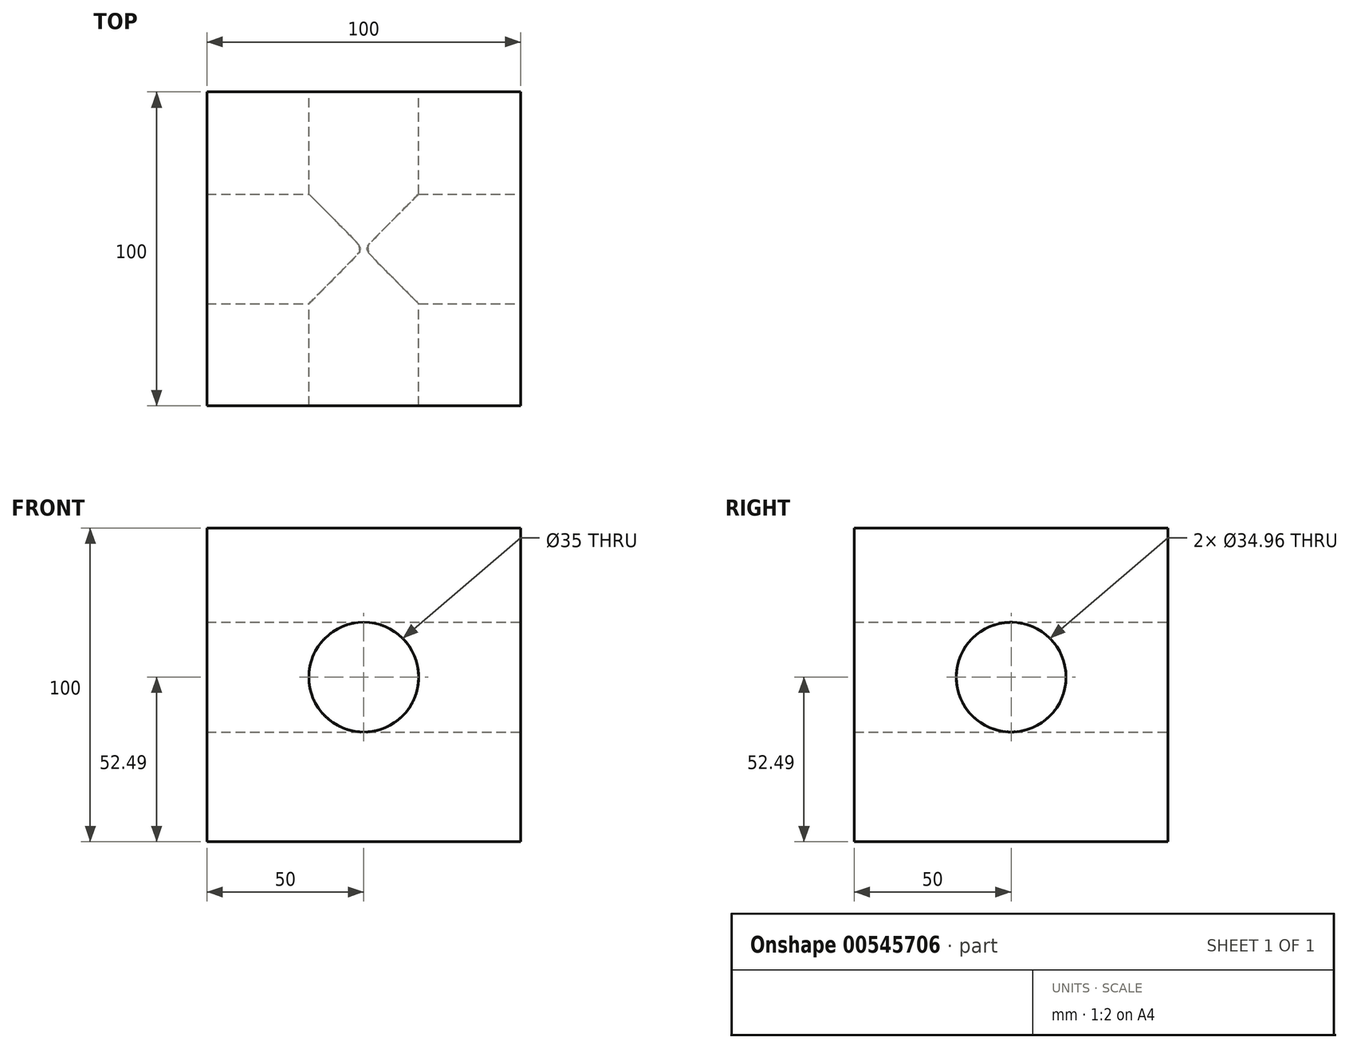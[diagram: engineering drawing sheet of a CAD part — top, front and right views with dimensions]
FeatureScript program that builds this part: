
annotation { "Feature Type Name" : "Feature", "Feature Type Description" : "" }
export const myFeature = defineFeature(function(context is Context, id is Id, definition is map)
    precondition{}
    {
        {
            var Q0;
            Q0=qCreatedBy(makeId("Front.planeOp"),FACE);
            var sketch = newSketch(context, id + "F0", { "sketchPlane" : qUnion([Q0])});
            skLineSegment(sketch, "E0.bottom", {"start": v(-50, 47.51) * mm, "end": v(50, 47.51) * mm});
            skLineSegment(sketch, "E0.top", {"start": v(-50, -52.49) * mm, "end": v(50, -52.49) * mm});
            skLineSegment(sketch, "E0.left", {"start": v(-50, 47.51) * mm, "end": v(-50, -52.49) * mm});
            skLineSegment(sketch, "E0.right", {"start": v(50, 47.51) * mm, "end": v(50, -52.49) * mm});
            skPoint(sketch, "E0.middle", {"position": v(0, -2.49) * mm});
            skSolve(sketch);
        }
        {
            var Q0;
            Q0=makeQuery(id+"F0.imprint","IMPRINT",FACE,{"disambiguationData":[TD([[makeQuery(id+"F0.imprint","IMPRINT",EDGE,{"derivedFrom":sQuery(id+"F0.wireOp",EDGE,"E0.bottom")}),-1.0]])]});
            extrude(context, id + "F1", {"entities" : qUnion([Q0]), "endBound" : BoundingType.SYMMETRIC, "depth" : 100 * mm, "offsetDistance" : 25 * mm});
        }
        {
            var Q0;
            Q0=qCreatedBy(makeId("Front.planeOp"),FACE);
            var sketch = newSketch(context, id + "F2", { "sketchPlane" : qUnion([Q0])});
            skCircle(sketch, "E1", {"center": v(0, 0) * mm, "radius": 17.5 * mm});
            skSolve(sketch);
        }
        {
            var Q0;
            Q0 = qSketchRegion(id + "F2", true);
            extrude(context, id + "F3", {"entities" : qUnion([Q0]), "operationType" : NewBodyOperationType.REMOVE, "endBound" : BoundingType.UP_TO_NEXT, "depth" : 25 * mm, "offsetDistance" : 25 * mm, "hasSecondDirection" : true, "secondDirectionOppositeDirection" : true, "secondDirectionDepth" : 110 * mm});
        }
        {
            var Q0;
            Q0=makeQuery(id+"F1.opExtrude","SWEPT_FACE",FACE,{"disambiguationData":[OSD([sQuery(id+"F0.wireOp",EDGE,"E0.right")])]});
            var sketch = newSketch(context, id + "F4", { "sketchPlane" : qUnion([Q0])});
            skCircle(sketch, "E2", {"center": v(0, 0) * mm, "radius": 17.48 * mm});
            skSolve(sketch);
        }
        {
            var Q0;
            Q0=makeQuery(id+"F4.imprint","IMPRINT",FACE,{"disambiguationData":[TD([[makeQuery(id+"F4.imprint","IMPRINT",EDGE,{"derivedFrom":sQuery(id+"F4.wireOp",EDGE,"E2")}),1.0]])]});
            var Q1;
            Q1=makeQuery(id+"F1.opExtrude","SWEPT_FACE",FACE,{"disambiguationData":[OSD([sQuery(id+"F0.wireOp",EDGE,"E0.left")])]});
            extrude(context, id + "F5", {"entities" : qUnion([Q0, Q1]), "operationType" : NewBodyOperationType.REMOVE, "endBound" : BoundingType.THROUGH_ALL, "oppositeDirection" : true, "depth" : 100 * mm, "hasOffset" : true, "offsetDistance" : 110 * mm});
        }
    });
